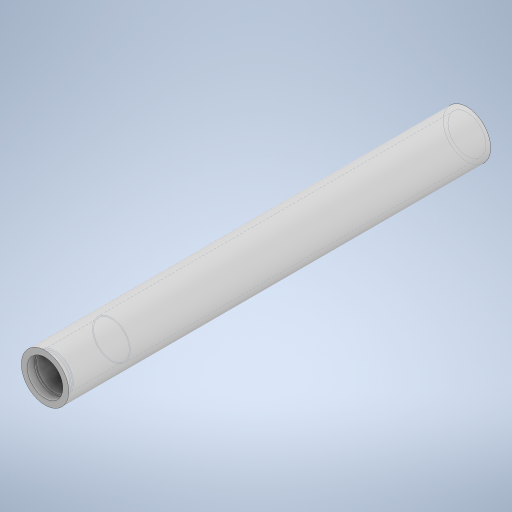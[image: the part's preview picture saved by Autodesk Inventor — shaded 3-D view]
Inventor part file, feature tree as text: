
AUTODESK INVENTOR PART (.ipt)
format: ipt  version: 2023 (Build 270158000, 158)  size: 265,216 bytes
history: native  units: mm
features: extrude x4, sketch x4, projected_geometry x4
ambient origin geometry x8: Origin, YZ Plane, XZ Plane, XY Plane, X Axis, Y Axis, Z Axis, Center Point
bodies: Solid1 (feature_tree)
feature tree (12):
  extrude  "Extrusion1"  Depth=20.0mm
  extrude  "Extrusion2"  Depth=24.0mm
  extrude  "Extrusion3"  Depth=150.0mm
  extrude  "Extrusion4"  Depth=3.0mm TaperAngle=0.0deg
  sketch  "Sketch1"  dims[d0=15.0mm d1=20.0mm]
  sketch  "Sketch2"  dims[d2=24.0mm d3=0.0mm d4=16.0mm]
  projected_geometry  "Projected Loop1"
  sketch  "Sketch3"  dims[d5=150.0mm d6=0.0mm d7=0.5mm]
  projected_geometry  "Projected Loop2"
  sketch  "Sketch4"  dims[d8=1.0mm d9=0.0mm d10=3.0mm d11=0.0mm]
  projected_geometry  "Project Cut Edges1"
  projected_geometry  "Project Cut Edges2"
